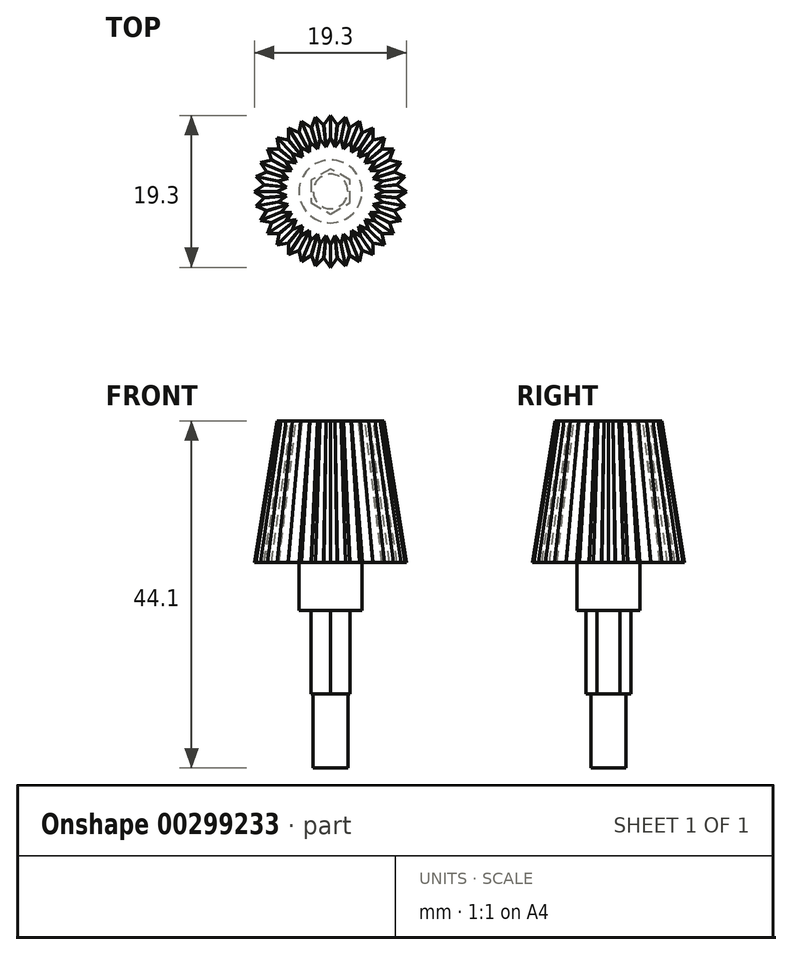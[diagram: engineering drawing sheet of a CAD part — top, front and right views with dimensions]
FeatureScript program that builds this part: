
annotation { "Feature Type Name" : "Feature", "Feature Type Description" : "" }
export const myFeature = defineFeature(function(context is Context, id is Id, definition is map)
    precondition{}
    {
        {
            var Q0;
            Q0=qCreatedBy(makeId("Top.planeOp"),FACE);
            var sketch = newSketch(context, id + "F0", { "sketchPlane" : qUnion([Q0])});
            skCircle(sketch, "E0", {"center": v(0, 0) * mm, "radius": 8.5 * mm});
            skSolve(sketch);
        }
        {
            var Q0;
            Q0 = qSketchRegion(id + "F0", true);
            extrude(context, id + "F1", {"entities" : qUnion([Q0]), "depth" : 18 * mm, "hasDraft" : true, "draftAngle" : 9 * degree, "draftPullDirection" : true});
        }
        {
            var Q0;
            Q0=qCreatedBy(makeId("Top.planeOp"),FACE);
            var sketch = newSketch(context, id + "F2", { "sketchPlane" : qUnion([Q0])});
            skLineSegment(sketch, "E1", {"start": v(0, 9.65) * mm, "end": v(-0.8, 8.46) * mm});
            skLineSegment(sketch, "E2", {"start": v(-0.8, 8.46) * mm, "end": v(0.8, 8.46) * mm});
            skLineSegment(sketch, "E3", {"start": v(0.8, 8.46) * mm, "end": v(0, 9.65) * mm});
            skSolve(sketch);
        }
        {
            var Q0;
            Q0=makeQuery(id+"F1.opExtrude","CAP_FACE",FACE,{"disambiguationData":[OSD([sQuery(id+"F0.wireOp",EDGE,"E0")])],"isStart":false});
            var sketch = newSketch(context, id + "F3", { "sketchPlane" : qUnion([Q0])});
            skLineSegment(sketch, "E4", {"start": v(0, 6.81) * mm, "end": v(-0.55, 5.62) * mm});
            skLineSegment(sketch, "E5", {"start": v(-0.55, 5.62) * mm, "end": v(0.55, 5.62) * mm});
            skLineSegment(sketch, "E6", {"start": v(0.55, 5.62) * mm, "end": v(0, 6.81) * mm});
            skSolve(sketch);
        }
        {
            var Q1;
            Q1=makeQuery(id+"F2.imprint","IMPRINT",FACE,{"disambiguationData":[TD([[makeQuery(id+"F2.imprint","IMPRINT",EDGE,{"derivedFrom":sQuery(id+"F2.wireOp",EDGE,"E1")}),1.0]])]});
            var Q2;
            {var subQ0=sQuery(id+"F3.wireOp",EDGE,"E4");Q2=makeQuery(id+"F3.imprint","IMPRINT",FACE,{"disambiguationData":[TD([[makeQuery(id+"F3.imprint","IMPRINT",EDGE,{"derivedFrom":subQ0}),1.0]])]});}
            loft(context, id + "F4", {"sheetProfilesArray" : [{ "sheetProfileEntities" : qUnion([Q1]) }, { "sheetProfileEntities" : qUnion([Q2]) }]});
        }
        {
            var Q0;
            Q0=qCreatedBy(makeId("Front.planeOp"),FACE);
            var sketch = newSketch(context, id + "F5", { "sketchPlane" : qUnion([Q0])});
            skLineSegment(sketch, "E7", {"start": v(0, 38.23) * mm, "end": v(0, -21.14) * mm, "construction": true});
            skSolve(sketch);
        }
        {
            var Q0;
            {var subQ0=sQuery(id+"F3.wireOp",EDGE,"E4");Q0=makeQuery(id+"F4.opLoft","SWEPT_BODY",BODY,{"disambiguationData":[OSD([makeQuery(id+"F2.imprint","IMPRINT",FACE,{"disambiguationData":[TD([[makeQuery(id+"F2.imprint","IMPRINT",EDGE,{"derivedFrom":sQuery(id+"F2.wireOp",EDGE,"E1")}),1.0]])]}),makeQuery(id+"F3.imprint","IMPRINT",FACE,{"disambiguationData":[TD([[makeQuery(id+"F3.imprint","IMPRINT",EDGE,{"derivedFrom":subQ0}),1.0]])]})])]});}
            var Q1;
            Q1=sQuery(id+"F5.wireOp",EDGE,"E7");
            circularPattern(context, id + "F6", {"operationType" : NewBodyOperationType.ADD, "entities" : qUnion([Q0]), "axis" : qUnion([Q1]), "angle" : 360 * degree, "instanceCount" : 32, "equalSpace" : true});
        }
        {
            var Q0;
            Q0=makeQuery(id+"F1.opExtrude","CAP_FACE",FACE,{"disambiguationData":[OSD([sQuery(id+"F0.wireOp",EDGE,"E0")])],"isStart":true});
            var sketch = newSketch(context, id + "F7", { "sketchPlane" : qUnion([Q0])});
            skCircle(sketch, "E8", {"center": v(0, 0) * mm, "radius": 4 * mm});
            skSolve(sketch);
        }
        {
            var Q0;
            Q0=makeQuery(id+"F7.imprint","IMPRINT",FACE,{"disambiguationData":[TD([[makeQuery(id+"F7.imprint","IMPRINT",EDGE,{"derivedFrom":sQuery(id+"F7.wireOp",EDGE,"E8")}),1.0]])]});
            var Q1;
            Q1=sQuery(id+"F7.wireOp",EDGE,"E8");
            extrude(context, id + "F8", {"entities" : qUnion([Q0]), "surfaceEntities" : qUnion([Q1]), "depth" : 6.1 * mm});
        }
        {
            var Q0;
            Q0=makeQuery(id+"F8.opExtrude","CAP_FACE",FACE,{"disambiguationData":[OSD([sQuery(id+"F7.wireOp",EDGE,"E8")])],"isStart":false});
            var sketch = newSketch(context, id + "F9", { "sketchPlane" : qUnion([Q0])});
            skCircle(sketch, "E9.cCircle", {"center": v(0, 0) * mm, "radius": 2.49 * mm, "construction": true});
            skLineSegment(sketch, "E9.0", {"start": v(-2.49, 1.44) * mm, "end": v(0, 2.87) * mm});
            skLineSegment(sketch, "E9.1", {"start": v(0, 2.87) * mm, "end": v(2.49, 1.44) * mm});
            skLineSegment(sketch, "E9.2", {"start": v(2.49, 1.43) * mm, "end": v(2.49, -1.44) * mm});
            skLineSegment(sketch, "E9.3", {"start": v(2.49, -1.44) * mm, "end": v(0, -2.87) * mm});
            skLineSegment(sketch, "E9.4", {"start": v(0, -2.87) * mm, "end": v(-2.49, -1.43) * mm});
            skLineSegment(sketch, "E9.5", {"start": v(-2.49, -1.43) * mm, "end": v(-2.49, 1.44) * mm});
            skPoint(sketch, "E9.0.midPoint", {"position": v(-1.24, 2.15) * mm});
            skLineSegment(sketch, "E10", {"start": v(0, 7.09) * mm, "end": v(0, -7) * mm, "construction": true});
            skSolve(sketch);
        }
        {
            var Q0;
            Q0=makeQuery(id+"F9.imprint","IMPRINT",FACE,{"disambiguationData":[TD([[makeQuery(id+"F9.imprint","IMPRINT",EDGE,{"derivedFrom":sQuery(id+"F9.wireOp",EDGE,"E9.0")}),-1.0]])]});
            extrude(context, id + "F10", {"entities" : qUnion([Q0]), "depth" : 10.6 * mm});
        }
        {
            var Q0;
            Q0=makeQuery(id+"F10.opExtrude","CAP_FACE",FACE,{"disambiguationData":[OSD([sQuery(id+"F9.wireOp",EDGE,"E9.0"),sQuery(id+"F9.wireOp",EDGE,"E9.1"),sQuery(id+"F9.wireOp",EDGE,"E9.2"),sQuery(id+"F9.wireOp",EDGE,"E9.3"),sQuery(id+"F9.wireOp",EDGE,"E9.4"),sQuery(id+"F9.wireOp",EDGE,"E9.5")])],"isStart":false});
            var sketch = newSketch(context, id + "F11", { "sketchPlane" : qUnion([Q0])});
            skCircle(sketch, "E11", {"center": v(0, 0) * mm, "radius": 2.2 * mm});
            skSolve(sketch);
        }
        {
            var Q0;
            Q0=makeQuery(id+"F11.imprint","IMPRINT",FACE,{"disambiguationData":[TD([[makeQuery(id+"F11.imprint","IMPRINT",EDGE,{"derivedFrom":sQuery(id+"F11.wireOp",EDGE,"E11")}),1.0]])]});
            extrude(context, id + "F12", {"entities" : qUnion([Q0]), "operationType" : NewBodyOperationType.ADD, "depth" : 9.4 * mm});
        }
    });
